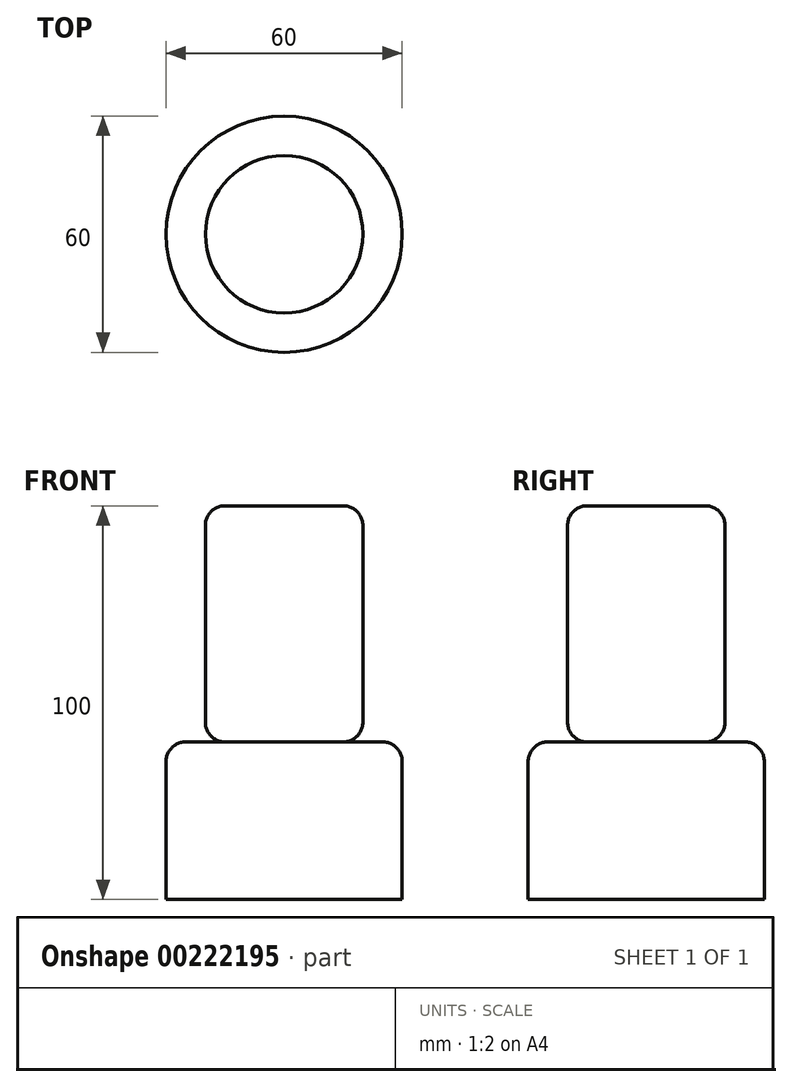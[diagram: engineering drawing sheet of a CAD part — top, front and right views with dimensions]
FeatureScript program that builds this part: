
annotation { "Feature Type Name" : "Feature", "Feature Type Description" : "" }
export const myFeature = defineFeature(function(context is Context, id is Id, definition is map)
    precondition{}
    {
        {
            var Q0;
            Q0=qCreatedBy(makeId("Top.planeOp"),FACE);
            var sketch = newSketch(context, id + "F0", { "sketchPlane" : qUnion([Q0])});
            skCircle(sketch, "E0", {"center": v(0, 0) * mm, "radius": 20 * mm});
            skCircle(sketch, "E1", {"center": v(0, 0) * mm, "radius": 30 * mm});
            skSolve(sketch);
        }
        {
            var Q0;
            Q0=makeQuery(id+"F0.imprint","IMPRINT",FACE,{"disambiguationData":[TD([[makeQuery(id+"F0.imprint","IMPRINT",EDGE,{"derivedFrom":sQuery(id+"F0.wireOp",EDGE,"E0")}),1.0]])]});
            extrude(context, id + "F1", {"entities" : qUnion([Q0]), "depth" : 60 * mm});
        }
        {
            var Q0;
            Q0=makeQuery(id+"F0.imprint","IMPRINT",FACE,{"disambiguationData":[TD([[makeQuery(id+"F0.imprint","IMPRINT",EDGE,{"derivedFrom":sQuery(id+"F0.wireOp",EDGE,"E0")}),-1.0]])]});
            var Q1;
            Q1=makeQuery(id+"F0.imprint","IMPRINT",FACE,{"disambiguationData":[TD([[makeQuery(id+"F0.imprint","IMPRINT",EDGE,{"derivedFrom":sQuery(id+"F0.wireOp",EDGE,"E0")}),1.0]])]});
            var Q2;
            Q2=sQuery(id+"F0.wireOp",EDGE,"E1");
            extrude(context, id + "F2", {"entities" : qUnion([Q0, Q1]), "surfaceEntities" : qUnion([Q2]), "oppositeDirection" : true, "depth" : 40 * mm});
        }
        {
            var Q0;
            Q0=makeQuery(id+"F1.opExtrude","CAP_EDGE",EDGE,{"disambiguationData":[OSD([sQuery(id+"F0.wireOp",EDGE,"E0")])],"isStart":false});
            fillet(context, id + "F3", {"entities" : qUnion([Q0]), "radius" : 5 * mm, "tangentPropagation" : true, "allowEdgeOverflow" : false});
        }
        {
            var Q0;
            Q0=makeQuery(id+"F2.opExtrude","CAP_EDGE",EDGE,{"disambiguationData":[OSD([sQuery(id+"F0.wireOp",EDGE,"E1")])],"isStart":true});
            fillet(context, id + "F4", {"entities" : qUnion([Q0]), "radius" : 5 * mm, "tangentPropagation" : true, "allowEdgeOverflow" : false});
        }
        {
            var Q0;
            Q0=makeQuery(id+"F1.opExtrude","CAP_EDGE",EDGE,{"disambiguationData":[OSD([sQuery(id+"F0.wireOp",EDGE,"E0")])],"isStart":true});
            fillet(context, id + "F5", {"entities" : qUnion([Q0]), "radius" : 5 * mm, "tangentPropagation" : true, "allowEdgeOverflow" : false});
        }
    });
